# Revit family: Bath-Freestanding-KOHLER-VOLUTE-K-20379T
name_source: partatom
category: Plumbing Fixtures
revit_build: Autodesk Revit 2017 (Build: 20160225_1515(x64)
units: mm (PartAtom-declared; Revit-internal decimal feet)

## family parameters
Cut with Voids When Loaded = No
Host = Face
OmniClass Number = 23.31.15.00
OmniClass Title = Bathtubs
Part Type = Normal
Room Calculation Point = No
Round Connector Dimension = Use Diameter
Shared = No

## types (4) — shared parameters
ADA Compliant = No
Assembly Code = D2010500
CW Connection = No
Cold Water Inlet = Cold Water Inlet
Date Modified = 01/29/2021
Default Elevation = 0"
Drain Included = No
HW Connection = No
Height = 23 1/4"
Hot Water Inlet = Hot Water Inlet
Length = 59 1/16"
Manufacturer = KOHLER Co.
Master Format 2014 = 22 41 19
Master Format 2014 Name = Residential Bathtubs
Material = Cast Iron
Product Documentation Link = https://files.kohler.com.cn
Product Name = VOLUTE
Product Page URL = https://www.kohler.com.cn
URL = http://www.kohler.com.cn
Vent Connection = No
Waste Connection = Yes
Waste Water Outlet = Waste Water Outlet
WaterSense Certified = No
Width = 31 1/2"

## per-type parameters (varying)
| type | Description | Finish | Model | Type |
| 0-White | Fule 1.5m Freestanding Cast Iron Bathtub (Rose Gold Skirt) | KOHLER-Cast_Iron-0-White | K-20379T-0 | 1 |
| GR,0-White | Fule 1.5m freestanding cast iron bathtub (rose gold skirt with handrail hole) | KOHLER-Cast_Iron-0-White | K-20379T-GR-0 | 2 |
| 7-Black Black | Fule 1.5m Freestanding Cast Iron Bathtub (Xuanwu Black) | KOHLER-Cast_Iron-7-Black_Black | K-20379T-7 | 3 |
| GR,7-Black Black | Fule 1.5m freestanding cast iron bathtub (with handrail hole, basalt black) | KOHLER-Cast_Iron-7-Black_Black | K-20379T-GR-7 | 4 |

## geometry (parser evidence)
native form markers: Sweep x6
no freeform markers — native parametric forms only
